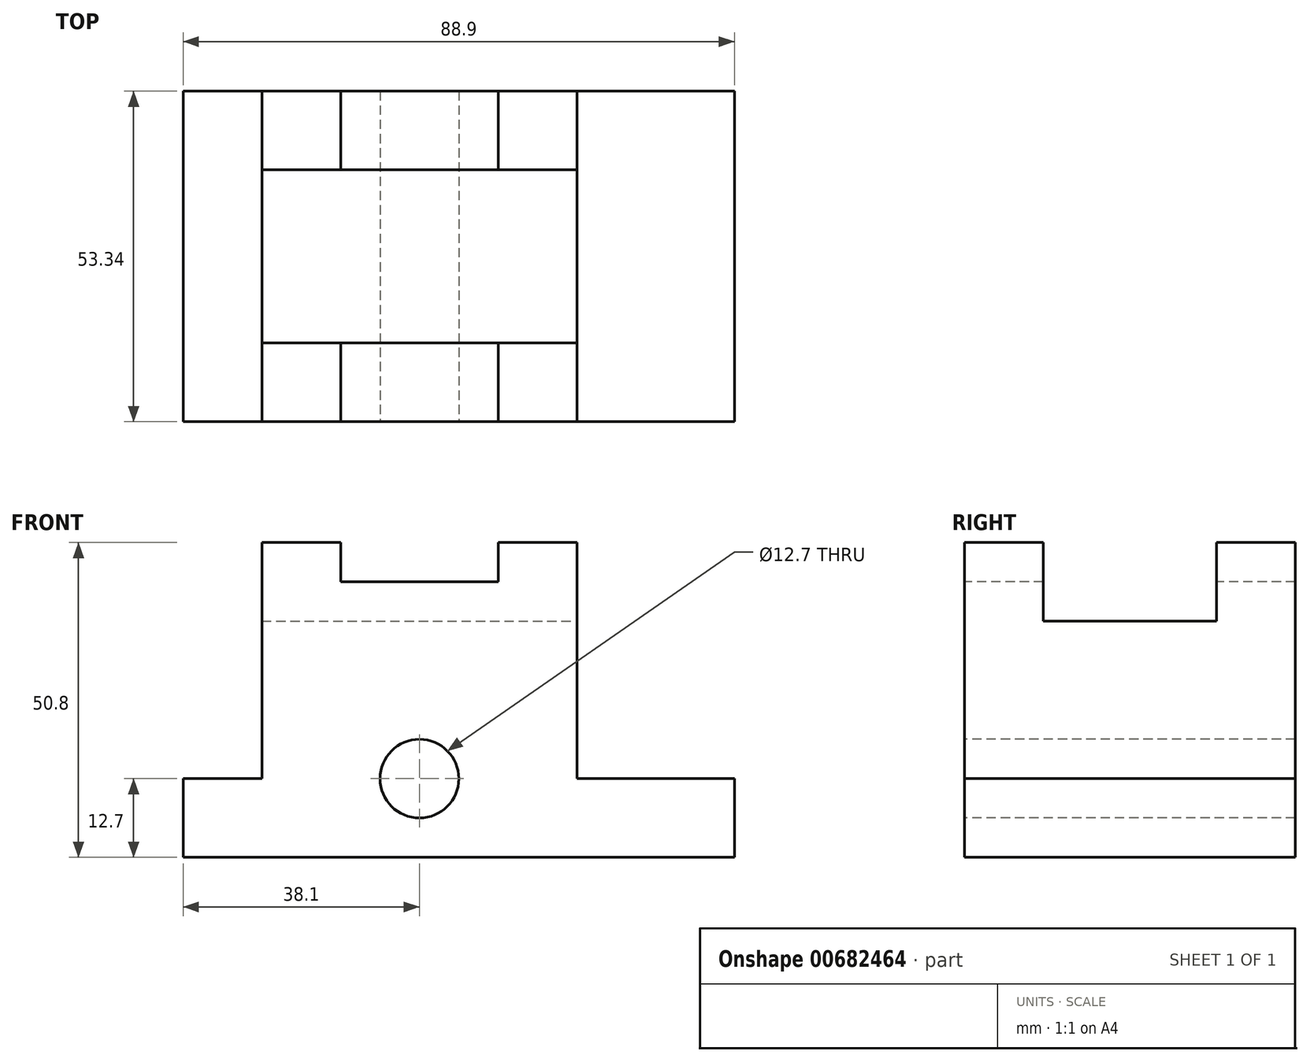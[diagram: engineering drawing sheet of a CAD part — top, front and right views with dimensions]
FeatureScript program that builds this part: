
annotation { "Feature Type Name" : "Feature", "Feature Type Description" : "" }
export const myFeature = defineFeature(function(context is Context, id is Id, definition is map)
    precondition{}
    {
        {
            var Q0;
            Q0=qCreatedBy(makeId("Front.planeOp"),FACE);
            var sketch = newSketch(context, id + "F0", { "sketchPlane" : qUnion([Q0])});
            skLineSegment(sketch, "E0.bottom", {"start": v(-44.45, 19.05) * mm, "end": v(44.45, 19.05) * mm});
            skLineSegment(sketch, "E0.top", {"start": v(-44.45, -19.05) * mm, "end": v(44.45, -19.05) * mm});
            skLineSegment(sketch, "E0.left", {"start": v(-44.45, 19.05) * mm, "end": v(-44.45, -19.05) * mm});
            skLineSegment(sketch, "E0.right", {"start": v(44.45, 19.05) * mm, "end": v(44.45, -19.05) * mm});
            skPoint(sketch, "E0.middle", {"position": v(0, 0) * mm});
            skSolve(sketch);
        }
        {
            var Q0;
            Q0=makeQuery(id+"F0.imprint","IMPRINT",FACE,{"disambiguationData":[TD([[makeQuery(id+"F0.imprint","IMPRINT",EDGE,{"derivedFrom":sQuery(id+"F0.wireOp",EDGE,"E0.bottom")}),-1.0]])]});
            extrude(context, id + "F1", {"entities" : qUnion([Q0]), "depth" : 53.34 * mm, "offsetDistance" : 25.4 * mm});
        }
        {
            var Q0;
            Q0=makeQuery(id+"F1.opExtrude","CAP_FACE",FACE,{"disambiguationData":[OSD([sQuery(id+"F0.wireOp",EDGE,"E0.bottom"),sQuery(id+"F0.wireOp",EDGE,"E0.top"),sQuery(id+"F0.wireOp",EDGE,"E0.left"),sQuery(id+"F0.wireOp",EDGE,"E0.right")])],"isStart":false});
            var sketch = newSketch(context, id + "F2", { "sketchPlane" : qUnion([Q0])});
            skLineSegment(sketch, "E1.bottom", {"start": v(-44.45, 19.05) * mm, "end": v(-31.75, 19.05) * mm});
            skLineSegment(sketch, "E1.top", {"start": v(-44.45, -6.35) * mm, "end": v(-31.75, -6.35) * mm});
            skLineSegment(sketch, "E1.left", {"start": v(-44.45, 19.05) * mm, "end": v(-44.45, -6.35) * mm});
            skLineSegment(sketch, "E1.right", {"start": v(-31.75, 19.05) * mm, "end": v(-31.75, -6.35) * mm});
            skSolve(sketch);
        }
        {
            var Q0;
            Q0=makeQuery(id+"F2.imprint","IMPRINT",FACE,{"disambiguationData":[TD([[makeQuery(id+"F2.imprint","IMPRINT",EDGE,{"derivedFrom":sQuery(id+"F2.wireOp",EDGE,"E1.bottom")}),-1.0]])]});
            extrude(context, id + "F3", {"entities" : qUnion([Q0]), "operationType" : NewBodyOperationType.REMOVE, "endBound" : BoundingType.THROUGH_ALL, "oppositeDirection" : true, "depth" : 25.4 * mm, "offsetDistance" : 25.4 * mm});
        }
        {
            var Q0;
            Q0=makeQuery(id+"F1.opExtrude","CAP_FACE",FACE,{"disambiguationData":[OSD([sQuery(id+"F0.wireOp",EDGE,"E0.bottom"),sQuery(id+"F0.wireOp",EDGE,"E0.top"),sQuery(id+"F0.wireOp",EDGE,"E0.left"),sQuery(id+"F0.wireOp",EDGE,"E0.right")])],"isStart":false});
            var sketch = newSketch(context, id + "F4", { "sketchPlane" : qUnion([Q0])});
            skLineSegment(sketch, "E2.bottom", {"start": v(44.45, 19.05) * mm, "end": v(19.05, 19.05) * mm});
            skLineSegment(sketch, "E2.top", {"start": v(44.45, -6.35) * mm, "end": v(19.05, -6.35) * mm});
            skLineSegment(sketch, "E2.left", {"start": v(44.45, 19.05) * mm, "end": v(44.45, -6.35) * mm});
            skLineSegment(sketch, "E2.right", {"start": v(19.05, 19.05) * mm, "end": v(19.05, -6.35) * mm});
            skSolve(sketch);
        }
        {
            var Q0;
            Q0=makeQuery(id+"F4.imprint","IMPRINT",FACE,{"disambiguationData":[TD([[makeQuery(id+"F4.imprint","IMPRINT",EDGE,{"derivedFrom":sQuery(id+"F4.wireOp",EDGE,"E2.bottom")}),-1.0]])]});
            extrude(context, id + "F5", {"entities" : qUnion([Q0]), "operationType" : NewBodyOperationType.REMOVE, "endBound" : BoundingType.THROUGH_ALL, "oppositeDirection" : true, "depth" : 25.4 * mm, "offsetDistance" : 25.4 * mm});
        }
        {
            var Q0;
            Q0=makeQuery(id+"F1.opExtrude","SWEPT_FACE",FACE,{"disambiguationData":[OSD([sQuery(id+"F0.wireOp",EDGE,"E0.bottom")])]});
            var sketch = newSketch(context, id + "F6", { "sketchPlane" : qUnion([Q0])});
            skLineSegment(sketch, "E3.bottom", {"start": v(-31.75, 0) * mm, "end": v(19.05, 0) * mm});
            skLineSegment(sketch, "E3.top", {"start": v(-31.75, -12.7) * mm, "end": v(19.05, -12.7) * mm});
            skLineSegment(sketch, "E3.left", {"start": v(-31.75, 0) * mm, "end": v(-31.75, -12.7) * mm});
            skLineSegment(sketch, "E3.right", {"start": v(19.05, 0) * mm, "end": v(19.05, -12.7) * mm});
            skLineSegment(sketch, "E4.bottom", {"start": v(-31.75, -53.34) * mm, "end": v(19.05, -53.34) * mm});
            skLineSegment(sketch, "E4.top", {"start": v(-31.75, -40.64) * mm, "end": v(19.05, -40.64) * mm});
            skLineSegment(sketch, "E4.left", {"start": v(-31.75, -53.34) * mm, "end": v(-31.75, -40.64) * mm});
            skLineSegment(sketch, "E4.right", {"start": v(19.05, -53.34) * mm, "end": v(19.05, -40.64) * mm});
            skSolve(sketch);
        }
        {
            var Q0;
            Q0=makeQuery(id+"F6.imprint","IMPRINT",FACE,{"disambiguationData":[TD([[makeQuery(id+"F6.imprint","IMPRINT",EDGE,{"derivedFrom":sQuery(id+"F6.wireOp",EDGE,"E3.bottom")}),-1.0]])]});
            var Q1;
            Q1=makeQuery(id+"F6.imprint","IMPRINT",FACE,{"disambiguationData":[TD([[makeQuery(id+"F6.imprint","IMPRINT",EDGE,{"derivedFrom":sQuery(id+"F6.wireOp",EDGE,"E4.bottom")}),1.0]])]});
            extrude(context, id + "F7", {"entities" : qUnion([Q0, Q1]), "operationType" : NewBodyOperationType.ADD, "depth" : 6.35 * mm, "offsetDistance" : 25.4 * mm});
        }
        {
            var Q0;
            Q0=makeQuery(id+"F7.opExtrude","CAP_FACE",FACE,{"disambiguationData":[OSD([sQuery(id+"F6.wireOp",EDGE,"E3.bottom"),sQuery(id+"F6.wireOp",EDGE,"E3.top"),sQuery(id+"F6.wireOp",EDGE,"E3.left"),sQuery(id+"F6.wireOp",EDGE,"E3.right")])],"isStart":false});
            var sketch = newSketch(context, id + "F8", { "sketchPlane" : qUnion([Q0])});
            skLineSegment(sketch, "E5.bottom", {"start": v(-19.05, 0) * mm, "end": v(6.35, 0) * mm});
            skLineSegment(sketch, "E5.top", {"start": v(-19.05, -12.7) * mm, "end": v(6.35, -12.7) * mm});
            skLineSegment(sketch, "E5.left", {"start": v(-19.05, 0) * mm, "end": v(-19.05, -12.7) * mm});
            skLineSegment(sketch, "E5.right", {"start": v(6.35, 0) * mm, "end": v(6.35, -12.7) * mm});
            skSolve(sketch);
        }
        {
            var Q0;
            Q0=makeQuery(id+"F7.opExtrude","CAP_FACE",FACE,{"disambiguationData":[OSD([sQuery(id+"F6.wireOp",EDGE,"E4.bottom"),sQuery(id+"F6.wireOp",EDGE,"E4.top"),sQuery(id+"F6.wireOp",EDGE,"E4.left"),sQuery(id+"F6.wireOp",EDGE,"E4.right")])],"isStart":false});
            var sketch = newSketch(context, id + "F9", { "sketchPlane" : qUnion([Q0])});
            skLineSegment(sketch, "E6.bottom", {"start": v(-19.05, -40.64) * mm, "end": v(6.35, -40.64) * mm});
            skLineSegment(sketch, "E6.top", {"start": v(-19.05, -53.34) * mm, "end": v(6.35, -53.34) * mm});
            skLineSegment(sketch, "E6.left", {"start": v(-19.05, -40.64) * mm, "end": v(-19.05, -53.34) * mm});
            skLineSegment(sketch, "E6.right", {"start": v(6.35, -40.64) * mm, "end": v(6.35, -53.34) * mm});
            skSolve(sketch);
        }
        {
            var Q0;
            {var subQ0=sQuery(id+"F9.wireOp",EDGE,"E6.left");Q0=makeQuery(id+"F9.imprint","IMPRINT",FACE,{"disambiguationData":[TD([[makeQuery(id+"F9.imprint","IMPRINT",EDGE,{"derivedFrom":subQ0}),-1.0]])]});}
            var Q1;
            {var subQ0=sQuery(id+"F8.wireOp",EDGE,"E5.left");Q1=makeQuery(id+"F8.imprint","IMPRINT",FACE,{"disambiguationData":[TD([[makeQuery(id+"F8.imprint","IMPRINT",EDGE,{"derivedFrom":subQ0}),-1.0]])]});}
            var Q2;
            {var subQ0=sQuery(id+"F8.wireOp",EDGE,"E5.right");Q2=makeQuery(id+"F8.imprint","IMPRINT",FACE,{"disambiguationData":[TD([[makeQuery(id+"F8.imprint","IMPRINT",EDGE,{"derivedFrom":subQ0}),1.0]])]});}
            var Q3;
            {var subQ0=sQuery(id+"F9.wireOp",EDGE,"E6.right");Q3=makeQuery(id+"F9.imprint","IMPRINT",FACE,{"disambiguationData":[TD([[makeQuery(id+"F9.imprint","IMPRINT",EDGE,{"derivedFrom":subQ0}),1.0]])]});}
            extrude(context, id + "F10", {"entities" : qUnion([Q0, Q1, Q2, Q3]), "operationType" : NewBodyOperationType.ADD, "depth" : 6.35 * mm, "offsetDistance" : 25.4 * mm});
        }
        {
            var Q0;
            {var subQ0=sQuery(id+"F6.wireOp",EDGE,"E4.bottom");var subQ1=makeQuery(id+"F7.opExtrude","CAP_EDGE",EDGE,{"disambiguationData":[OSD([subQ0])],"isStart":false});Q0=makeQuery(id+"F10.boolean.opBoolean","MERGE",FACE,{"derivedFrom":[makeQuery(id+"F7.boolean.opBoolean","MERGE",FACE,{"derivedFrom":[makeQuery(id+"F1.opExtrude","CAP_FACE",FACE,{"disambiguationData":[OSD([sQuery(id+"F0.wireOp",EDGE,"E0.bottom"),sQuery(id+"F0.wireOp",EDGE,"E0.top"),sQuery(id+"F0.wireOp",EDGE,"E0.left"),sQuery(id+"F0.wireOp",EDGE,"E0.right")])],"isStart":false}),makeQuery(id+"F7.opExtrude","SWEPT_FACE",FACE,{"disambiguationData":[OSD([subQ0])]})]}),makeQuery(id+"F10.opExtrude","SWEPT_FACE",FACE,{"disambiguationData":[OSD([subQ0]),TDD([makeQuery(id+"F9.imprint","IMPRINT",EDGE,{"disambiguationData":[TD([[makeQuery(id+"F9.imprint","INTERSECT",VERTEX,{"derivedFrom":[subQ1,makeQuery(id+"F7.opExtrude","CAP_EDGE",EDGE,{"disambiguationData":[OSD([sQuery(id+"F6.wireOp",EDGE,"E4.left")])],"isStart":false})]}),-1.0]])],"derivedFrom":subQ1})])]}),makeQuery(id+"F10.opExtrude","SWEPT_FACE",FACE,{"disambiguationData":[OSD([subQ0]),TDD([makeQuery(id+"F9.imprint","IMPRINT",EDGE,{"disambiguationData":[TD([[makeQuery(id+"F9.imprint","INTERSECT",VERTEX,{"derivedFrom":[subQ1,makeQuery(id+"F7.opExtrude","CAP_EDGE",EDGE,{"disambiguationData":[OSD([sQuery(id+"F6.wireOp",EDGE,"E4.right")])],"isStart":false})]}),1.0]])],"derivedFrom":subQ1})])]})]});}
            var sketch = newSketch(context, id + "F11", { "sketchPlane" : qUnion([Q0])});
            skCircle(sketch, "E7", {"center": v(-6.35, -6.35) * mm, "radius": 6.35 * mm});
            skSolve(sketch);
        }
        {
            var Q0;
            Q0=makeQuery(id+"F11.imprint","IMPRINT",FACE,{"disambiguationData":[TD([[makeQuery(id+"F11.imprint","IMPRINT",EDGE,{"derivedFrom":sQuery(id+"F11.wireOp",EDGE,"E7")}),1.0]])]});
            extrude(context, id + "F12", {"entities" : qUnion([Q0]), "operationType" : NewBodyOperationType.REMOVE, "endBound" : BoundingType.THROUGH_ALL, "oppositeDirection" : true, "depth" : 25.4 * mm, "offsetDistance" : 25.4 * mm});
        }
    });
